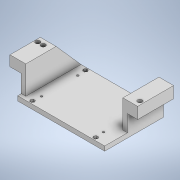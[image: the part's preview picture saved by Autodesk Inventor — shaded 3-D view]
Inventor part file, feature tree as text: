
AUTODESK INVENTOR PART (.ipt)
format: ipt  version: 2020 (Build 240168000, 168)  size: 229,376 bytes
history: native  units: mm
features: other x4, mirror x1
ambient origin geometry x8: Origin, YZ Plane, XZ Plane, XY Plane, X Axis, Y Axis, Z Axis, Center Point
bodies: Body1 (feature_tree)
feature tree (5):
  other  "tray_R_final.ipt"
  mirror  "미러1"
  other  "솔리드1::tray_R_final.ipt"
  other  "피쳐 태그1"
  other  "솔리드1"
